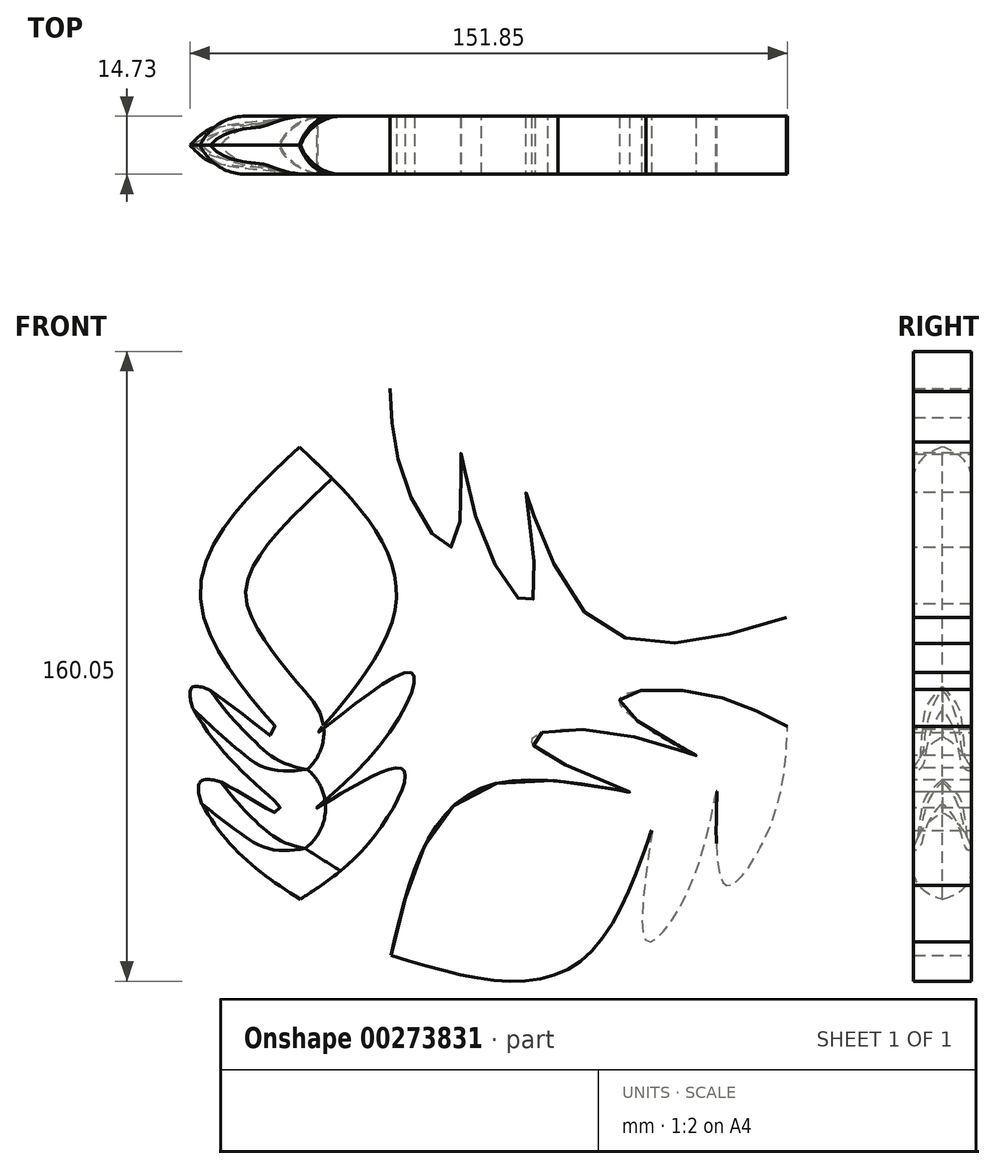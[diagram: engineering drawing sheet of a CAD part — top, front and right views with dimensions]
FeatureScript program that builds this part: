
annotation { "Feature Type Name" : "Feature", "Feature Type Description" : "" }
export const myFeature = defineFeature(function(context is Context, id is Id, definition is map)
    precondition{}
    {
        {
            var Q0;
            Q0=qCreatedBy(makeId("Front.planeOp"),FACE);
            var sketch = newSketch(context, id + "F0", { "sketchPlane" : qUnion([Q0])});
            skLineSegment(sketch, "E0", {"start": v(0, 71.05) * mm, "end": v(0, -72.23) * mm, "construction": true});
            skFitSpline(sketch, "E1", {"points": [v(0, 58.06) * mm, v(-24.67, 13.74) * mm, v(-5.76, -15.2) * mm, v(-28.5, 0) * mm, v(-21.12, -18.75) * mm, v(-5.47, -34.41) * mm, v(-26.44, -24.37) * mm, v(-20.24, -41.2) * mm, v(0, -58.34) * mm], "startDerivative": vector(-256.62, -241.1) * mm, "endDerivative": vector(169.47, -108.43) * mm});
            skFitSpline(sketch, "E2.MirrorCS", {"points": [v(0, 58.06) * mm, v(24.67, 13.74) * mm, v(5.76, -15.2) * mm, v(28.5, 0) * mm, v(21.12, -18.75) * mm, v(5.47, -34.41) * mm, v(26.44, -24.37) * mm, v(20.24, -41.2) * mm, v(0, -58.34) * mm], "startDerivative": vector(256.62, -241.1) * mm, "endDerivative": vector(-169.47, -108.43) * mm});
            skSolve(sketch);
        }
        {
            var Q0;
            Q0=qCreatedBy(makeId("Front.planeOp"),FACE);
            var sketch = newSketch(context, id + "F1", { "sketchPlane" : qUnion([Q0])});
            skPoint(sketch, "E3.0.internal.orphan", {"position": v(0, 57.57) * mm});
            skPoint(sketch, "E3.5.internal.orphan", {"position": v(0, 72.9) * mm});
            skSolve(sketch);
        }
        {
            var Q0;
            Q0 = qSketchRegion(id + "F1", true);
            var Q1;
            Q1=makeQuery(id+"F0.imprint","IMPRINT",FACE,{"disambiguationData":[TD([[makeQuery(id+"F0.imprint","IMPRINT",EDGE,{"derivedFrom":sQuery(id+"F0.wireOp",EDGE,"E1")}),1.0]])]});
            extrude(context, id + "F2", {"entities" : qUnion([Q0, Q1]), "depth" : 14.73 * mm});
        }
        {
            var Q0;
            Q0=qCreatedBy(makeId("Top.planeOp"),FACE);
            var sketch = newSketch(context, id + "F3", { "sketchPlane" : qUnion([Q0])});
            skLineSegment(sketch, "E4", {"start": v(49.57, 55.62) * mm, "end": v(49.57, -58.7) * mm, "construction": true});
            skSolve(sketch);
        }
        {
            var Q0;
            Q0=makeQuery(id+"F2.opExtrude","SWEPT_BODY",BODY,{"disambiguationData":[OSD([sQuery(id+"F0.wireOp",EDGE,"E1"),sQuery(id+"F0.wireOp",EDGE,"E2.MirrorCS")])]});
            var Q1;
            Q1=sQuery(id+"F3.wireOp",EDGE,"E4");
            circularPattern(context, id + "F4", {"entities" : qUnion([Q0]), "axis" : qUnion([Q1]), "angle" : 360 * degree, "instanceCount" : 3, "equalSpace" : true});
        }
        {
            var Q0;
            Q0=makeQuery(id+"F2.opExtrude","CAP_EDGE",EDGE,{"disambiguationData":[OSD([sQuery(id+"F0.wireOp",EDGE,"E1")])],"isStart":false});
            var Q1;
            Q1=makeQuery(id+"F2.opExtrude","CAP_EDGE",EDGE,{"disambiguationData":[OSD([sQuery(id+"F0.wireOp",EDGE,"E1")])],"isStart":true});
            fillet(context, id + "F5", {"entities" : qUnion([Q0, Q1]), "radius" : 12.7 * mm, "tangentPropagation" : true, "allowEdgeOverflow" : false});
        }
    });
